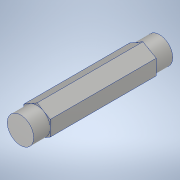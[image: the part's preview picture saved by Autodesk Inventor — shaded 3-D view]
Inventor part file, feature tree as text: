
AUTODESK INVENTOR PART (.ipt)
format: ipt  version: 2020 (Build 240168000, 168)  size: 135,168 bytes
history: native  units: in
note: dims shown in document units (in); Inventor stores cm internally (conversion verified against a paired STEP export)
features: extrude x2, sketch x2, mirror x1, projected_geometry x1
ambient origin geometry x8: Origin, YZ Plane, XZ Plane, XY Plane, X Axis, Y Axis, Z Axis, Center Point
bodies: Solid1 (feature_tree)
feature tree (6):
  extrude  "Extrusion1"  TaperAngle=0.0deg  [1 undecoded]
  extrude  "Extrusion2"  [1 undecoded]
  mirror  "Mirror1"
  sketch  "Sketch1"  dims[d2=0.0in d4=0.0in]
  sketch  "Sketch2"
  projected_geometry  "Projected Loop1"
note: 2 required parameter values undecoded (feature->parameter linkage not recoverable at this tier; creation-order binding heuristic only, values carry confidence <= 0.55)
